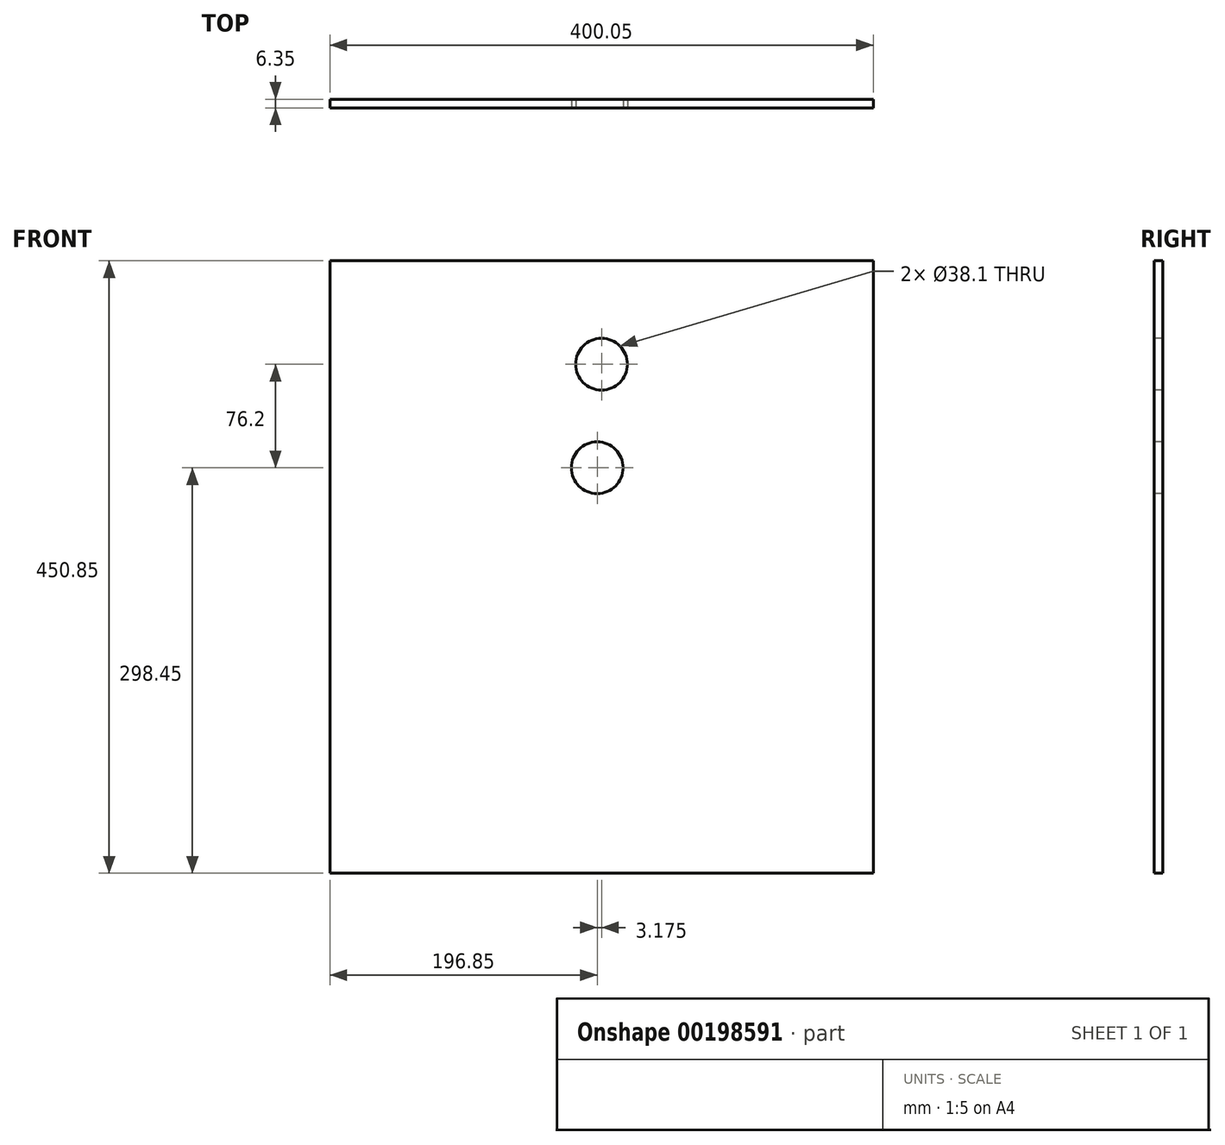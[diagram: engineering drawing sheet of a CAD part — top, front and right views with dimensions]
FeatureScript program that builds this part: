
annotation { "Feature Type Name" : "Feature", "Feature Type Description" : "" }
export const myFeature = defineFeature(function(context is Context, id is Id, definition is map)
    precondition{}
    {
        {
            var Q0;
            Q0=qCreatedBy(makeId("Front.planeOp"),FACE);
            var sketch = newSketch(context, id + "F0", { "sketchPlane" : qUnion([Q0])});
            skLineSegment(sketch, "E0.bottom", {"start": v(0, 0) * mm, "end": v(400.05, 0) * mm});
            skLineSegment(sketch, "E0.top", {"start": v(0, 450.85) * mm, "end": v(400.05, 450.85) * mm});
            skLineSegment(sketch, "E0.left", {"start": v(0, 0) * mm, "end": v(0, 450.85) * mm});
            skLineSegment(sketch, "E0.right", {"start": v(400.05, 0) * mm, "end": v(400.05, 450.85) * mm});
            skSolve(sketch);
        }
        {
            var Q0;
            Q0 = qSketchRegion(id + "F0", true);
            extrude(context, id + "F1", {"entities" : qUnion([Q0]), "depth" : 6.35 * mm});
        }
        {
            var Q0;
            Q0=makeQuery(id+"F1.opExtrude","CAP_FACE",FACE,{"disambiguationData":[OSD([sQuery(id+"F0.wireOp",EDGE,"E0.bottom"),sQuery(id+"F0.wireOp",EDGE,"E0.top"),sQuery(id+"F0.wireOp",EDGE,"E0.left"),sQuery(id+"F0.wireOp",EDGE,"E0.right")])],"isStart":false});
            var sketch = newSketch(context, id + "F2", { "sketchPlane" : qUnion([Q0])});
            skPoint(sketch, "E1.endSnap0", {"position": v(200.02, 450.85) * mm});
            skCircle(sketch, "E2", {"center": v(200.02, 374.65) * mm, "radius": 19.05 * mm});
            skCircle(sketch, "E3", {"center": v(196.85, 298.45) * mm, "radius": 19.05 * mm});
            skSolve(sketch);
        }
        {
            var Q0;
            Q0 = qSketchRegion(id + "F2", true);
            extrude(context, id + "F3", {"entities" : qUnion([Q0]), "operationType" : NewBodyOperationType.REMOVE, "oppositeDirection" : true, "depth" : 25.4 * mm});
        }
    });
